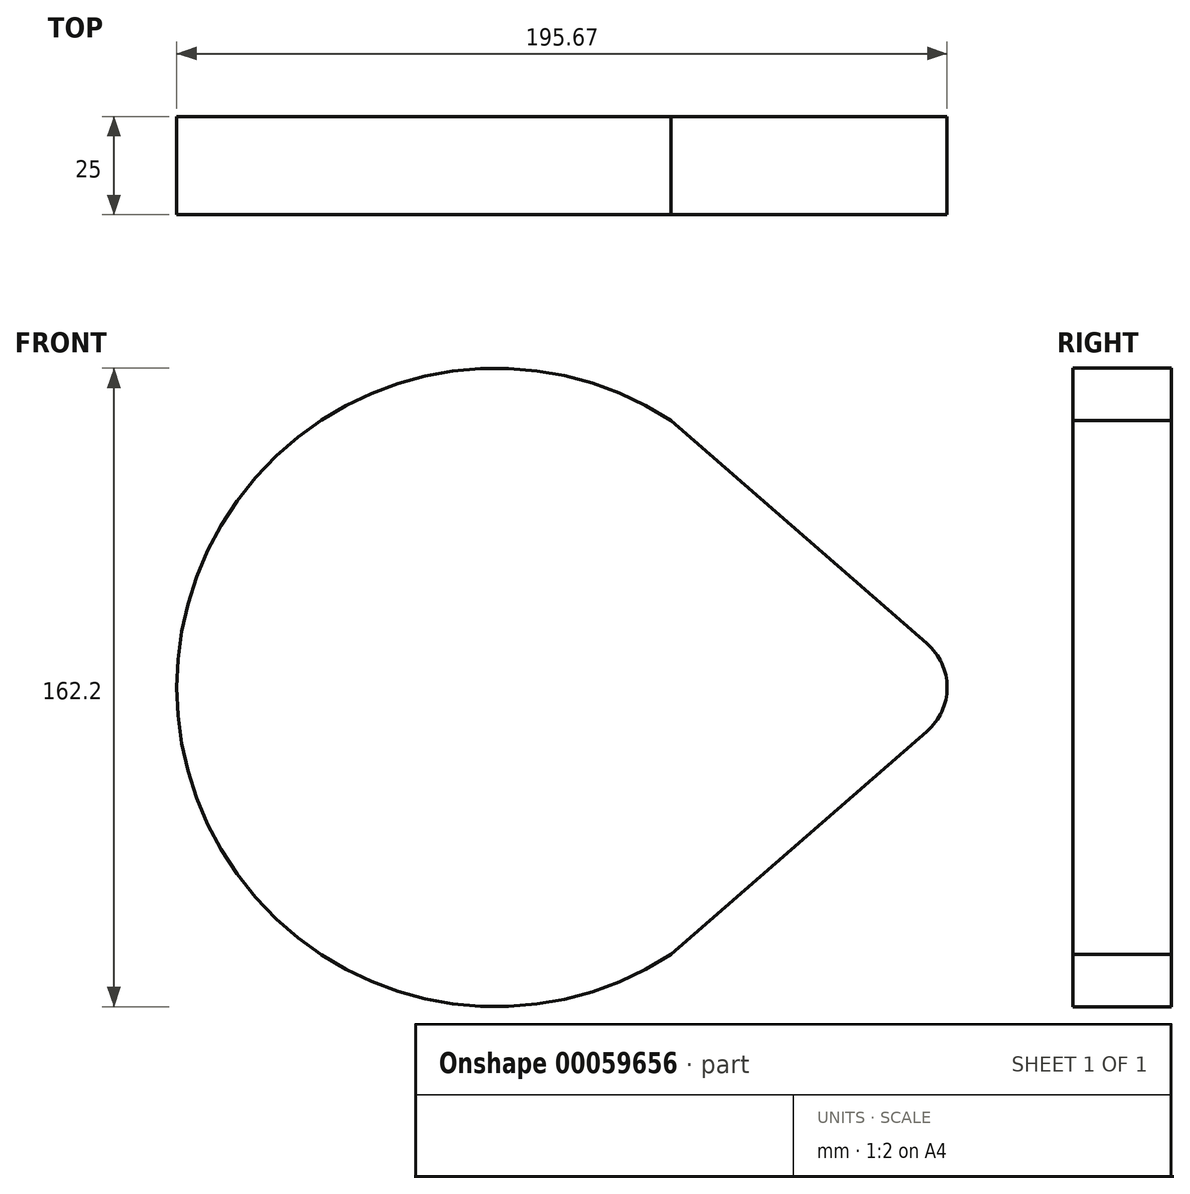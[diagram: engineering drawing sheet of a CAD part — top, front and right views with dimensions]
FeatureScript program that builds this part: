
annotation { "Feature Type Name" : "Feature", "Feature Type Description" : "" }
export const myFeature = defineFeature(function(context is Context, id is Id, definition is map)
    precondition{}
    {
        {
            var Q0;
            Q0=qCreatedBy(makeId("Front.planeOp"),FACE);
            var sketch = newSketch(context, id + "F0", { "sketchPlane" : qUnion([Q0])});
            skArc(sketch, "E0", {"start": v(0, 67.8) * mm, "mid": v(-125.6, 0) * mm, "end": v(0, -67.8) * mm});
            skArc(sketch, "E1", {"start": v(65.01, -11.13) * mm, "mid": v(70.07, 0) * mm, "end": v(65.01, 11.13) * mm});
            skLineSegment(sketch, "E2", {"start": v(0, 67.8) * mm, "end": v(65.01, 11.13) * mm});
            skLineSegment(sketch, "E3", {"start": v(65.01, 11.13) * mm, "end": v(65.01, 11.13) * mm});
            skLineSegment(sketch, "E4", {"start": v(0, -67.8) * mm, "end": v(65.01, -11.13) * mm});
            skSolve(sketch);
        }
        {
            var Q0;
            Q0=makeQuery(id+"F0.imprint","IMPRINT",FACE,{"disambiguationData":[TD([[makeQuery(id+"F0.imprint","IMPRINT",EDGE,{"derivedFrom":sQuery(id+"F0.wireOp",EDGE,"E0")}),1.0]])]});
            extrude(context, id + "F1", {"entities" : qUnion([Q0]), "depth" : 25 * mm});
        }
    });
